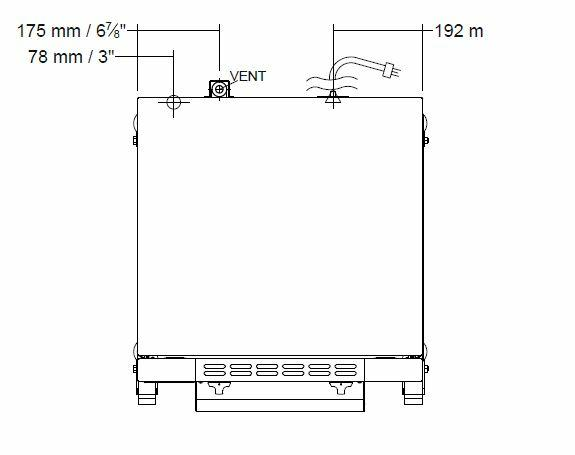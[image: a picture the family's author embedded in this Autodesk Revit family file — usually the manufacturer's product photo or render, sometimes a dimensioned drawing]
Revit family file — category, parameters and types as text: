
# Revit family: QF_MOFFAT_E28D4-2_NZ
name_source: partatom
category: Specialty Equipment
revit_build: Autodesk Revit 2014 (Build: 20130308_1515(x64)
units: mm (PartAtom-declared; Revit-internal decimal feet)

## types (1)
- QF_MOFFAT_E28D4-2_NZ
    Apparent Power = 5750 VA
    Cold Water Connection Height = 0 mm  [stored 0 ft]
    Cold Water Flow = 0 GPM
    Cold Water Maximum Pressure = 80.00 psi
    Cold Water Minimum Pressure = 20.00 psi
    Cold Water RI Height = 0 mm  [stored 0 ft]
    Cold Water Size = 1"
    Cold Water Temperature Recommended = 0 °F
    Conn Conduit = Yes
    Cycle = 50 Hz
    Depth = 762 mm  [stored 2.5 ft]
    Description = FULL SIZE DIGITAL / ELECTRIC CONVECTION OVENS DOUBLE STACKED ON A STAINLESS STEEL BASE STAND
    Elec Conn Connection Height = 0 mm  [stored 0 ft]
    Elec Conn RI Height = 0 mm  [stored 0 ft]
    Electrical Remarks = 230-240V, 50Hz, 1P+N+E, 5.8kW, 25A
    Exhaust RI Height = 0 mm  [stored 0 ft]
    Exhaust Static Press = 0.00 in-wg
    Exhaust Vent Depth = 0 mm  [stored 0 ft]
    Exhaust Vent Diameter = 0 mm  [stored 0 ft]
    Exhaust Vent Width = 0 mm  [stored 0 ft]
    Exhaust Volume = 0 CFM
    FL Amps = 25 A
    Foodservice Equipment Identifier = Yes
    Height = 1681 mm  [stored 5.51509 ft]
    Height of Stand = 454 mm  [stored 1.4895 ft]
    Identify Quantity as Lot = Yes
    Length = 810 mm  [stored 2.65748 ft]
    Manufacturer = MOFFAT
    Max Overcurrent Protection = 0 A
    Min Ckt Ampacity = 0 A
    Model = E28D4-2
    Number of Poles = 1
    Phase = 1
    URL = www.moffat.com.au
    URL Cutsheet = www.moffat.com.au
    Volts = 230 V
    Watts = 5800 W
    Weight in Pounds = 0

note: [stored X ft] marks values corroborated as IEEE doubles in the binary element streams (Revit-internal decimal feet)

## geometry (parser evidence)
native form markers: Blend x16, Sweep x10
no freeform markers — native parametric forms only
